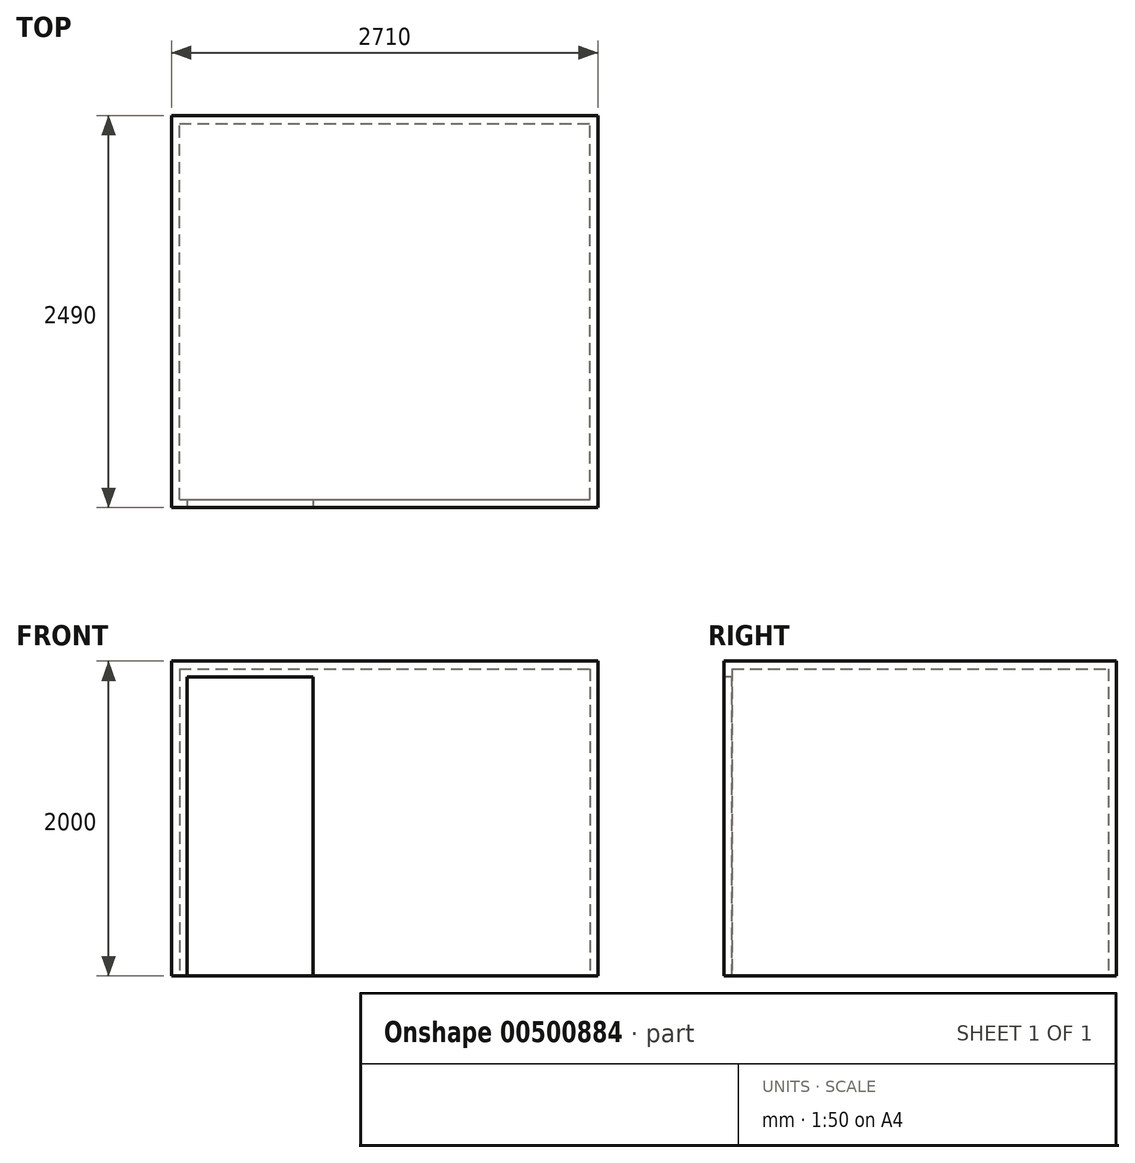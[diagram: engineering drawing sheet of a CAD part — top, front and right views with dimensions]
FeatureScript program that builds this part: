
annotation { "Feature Type Name" : "Feature", "Feature Type Description" : "" }
export const myFeature = defineFeature(function(context is Context, id is Id, definition is map)
    precondition{}
    {
        {
            var Q0;
            Q0=qCreatedBy(makeId("Top.planeOp"),FACE);
            var sketch = newSketch(context, id + "F0", { "sketchPlane" : qUnion([Q0])});
            skLineSegment(sketch, "E0.bottom", {"start": v(0, 0) * mm, "end": v(2710, 0) * mm});
            skLineSegment(sketch, "E0.top", {"start": v(0, 2490) * mm, "end": v(2710, 2490) * mm});
            skLineSegment(sketch, "E0.left", {"start": v(0, 0) * mm, "end": v(0, 2490) * mm});
            skLineSegment(sketch, "E0.right", {"start": v(2710, 0) * mm, "end": v(2710, 2490) * mm});
            skSolve(sketch);
        }
        {
            var Q0;
            Q0 = qSketchRegion(id + "F0", true);
            extrude(context, id + "F1", {"entities" : qUnion([Q0]), "depth" : 2000 * mm});
        }
        {
            var Q0;
            Q0=makeQuery(id+"F1.opExtrude","CAP_FACE",FACE,{"disambiguationData":[OSD([sQuery(id+"F0.wireOp",EDGE,"E0.bottom"),sQuery(id+"F0.wireOp",EDGE,"E0.top"),sQuery(id+"F0.wireOp",EDGE,"E0.left"),sQuery(id+"F0.wireOp",EDGE,"E0.right")])],"isStart":true});
            shell(context, id + "F2", {"entities" : qUnion([Q0]), "thickness" : 50 * mm});
        }
        {
            var Q0;
            Q0=makeQuery(id+"F1.opExtrude","SWEPT_FACE",FACE,{"disambiguationData":[OSD([sQuery(id+"F0.wireOp",EDGE,"E0.bottom")])]});
            var sketch = newSketch(context, id + "F3", { "sketchPlane" : qUnion([Q0])});
            skLineSegment(sketch, "E1.bottom", {"start": v(100, 0) * mm, "end": v(900, 0) * mm});
            skLineSegment(sketch, "E1.top", {"start": v(100, 1900) * mm, "end": v(900, 1900) * mm});
            skLineSegment(sketch, "E1.left", {"start": v(100, 0) * mm, "end": v(100, 1900) * mm});
            skLineSegment(sketch, "E1.right", {"start": v(900, 0) * mm, "end": v(900, 1900) * mm});
            skSolve(sketch);
        }
        {
            var Q0;
            Q0 = qSketchRegion(id + "F3", true);
            extrude(context, id + "F4", {"entities" : qUnion([Q0]), "operationType" : NewBodyOperationType.REMOVE, "endBound" : BoundingType.UP_TO_NEXT, "oppositeDirection" : true, "depth" : 25 * mm});
        }
    });
